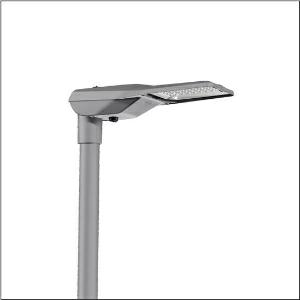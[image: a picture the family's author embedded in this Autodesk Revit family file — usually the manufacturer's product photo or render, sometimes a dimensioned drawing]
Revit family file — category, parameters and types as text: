
# Revit family: streetlight_sl_21_iq_mini___st1_0a_5xe2d41y08hb_48d2
name_source: partatom
category: Lighting Fixtures
units: mm (PartAtom-declared; Revit-internal decimal feet)

## family parameters
Cut with Voids When Loaded = No
Host = Face
Light Source = No
Part Type = Normal
Room Calculation Point = No
Round Connector Dimension = Use Diameter
Shared = No

## types (1)
- --- (1 x LED, 10080 lm, 71 W, 4000K)
    Apparent Load = 71 VA
    CIE Flux Codes = 37 72 97 100 100
    Color Rendering = 70
    Color Temperature = 4000K
    Default Elevation = 1800 mm
    Description = Streetlight SL 21 iQ mini, mast luminaire, primary light control with lens, of PMMA, primary optical cover: cover, of toughened safety glass, transparent, light distribution: ST1.0a, light emission: direct distribution, primary light characteristic: asymmetric, installation type: post-top, side-entry, LED, High Power LED, rated luminous flux: 10.080lm, luminous efficacy: 142lm/W, light colour: 740, colour temperature: 4000K, control: presetting dimming logarithmic, Street-Remote, Auto-Match, Temp-Guard, Lumen-Switch, Night-Set, Smart-Wire, Light-Fading, Desk-Remote (wireless, voltage-free reading and setting of iQ features in the workshop via application-optimized NFC function/RFID function), optimised constant luminous flux control (CLO 2.0), mains connection: 220..240V, AC, 50/60Hz, start of lifetime: 71W, end of service life: 75W, reduction: 31W, luminaire housing, of diecast aluminium, powder-coated, Siteco® metallic grey (DB 702S), corrosivity category C5 mid according to DIN EN ISO 12944, please order mast flange separately, inclination adjustable: 0°, 5°, 10°, 15°, sealing non-destructively replaceable, multi-level sealing system, length: 628mm, width: 235mm, height: 110mm, mast flange for spigot size: 42mm (side-entry): 5XC10008XM4, 60/48mm (side-entry/post-top): 5XC10108XM2, 76/60mm (side-entry/post-top): 5XC10108XM1, Smart Interface below and above, protection rating (complete): IP66, insulation class (complete): insulation class II (safety insulation), certification: CE, ENEC, ENEC+, VDE, impact resistance: IK09, permissible operating ambient temperature for outdoor applications: -40..+50°C, standard-compliant lighting for roads and squares, packaging unit: 1 piece

Light Distribution: ST1.0a
    Height = 110 mm
    Lamp = 1 x LED
    Lamp Light Flux = 10080 lm
    Lamp Power = 71 W
    Lamp count = 1
    Length = 625 mm
    Luminous efficacy = 142 lm/W
    Manufacturer = Siteco
    ModVariant = No
    Model = 5XE2D41Y08HB
    Number of Poles = 1
    OnlyDefault = Yes
    Power Factor = 1
    Product Name = Streetlight SL 21 iQ mini | ST1.0a
    Product group = mast luminaire | pylon top
    ProductGroupID = 6100
    Protection Class = Protection class II
    Protection Degree = IP 66
    RLX_Detail_Level = 1
    RLX_Emergency_Light_Flux = 0 lm
    RLX_Emergency_Type = 0
    RLX_Emergency_Type_DB = No
    RlxData = <blob elided: 92321 chars, md5=42279707>
    Socket = socket
    Standby Power = 0 W
    System Light Flux = 10080 lm
    System Power = 71 W
    Type Comments = factory setting: luminous flux: 100 % | dim-lin: 254 | 716 mA
    Type Image = l_1003514.jpg
    URL = http://relux.com
    VarID = @adj_062917
    Voltage = 0 V
    Weight = 0.00 kg
    Width = 234 mm

## geometry (parser evidence)
native form markers: Blend x4, Sweep x12
no freeform markers — native parametric forms only
